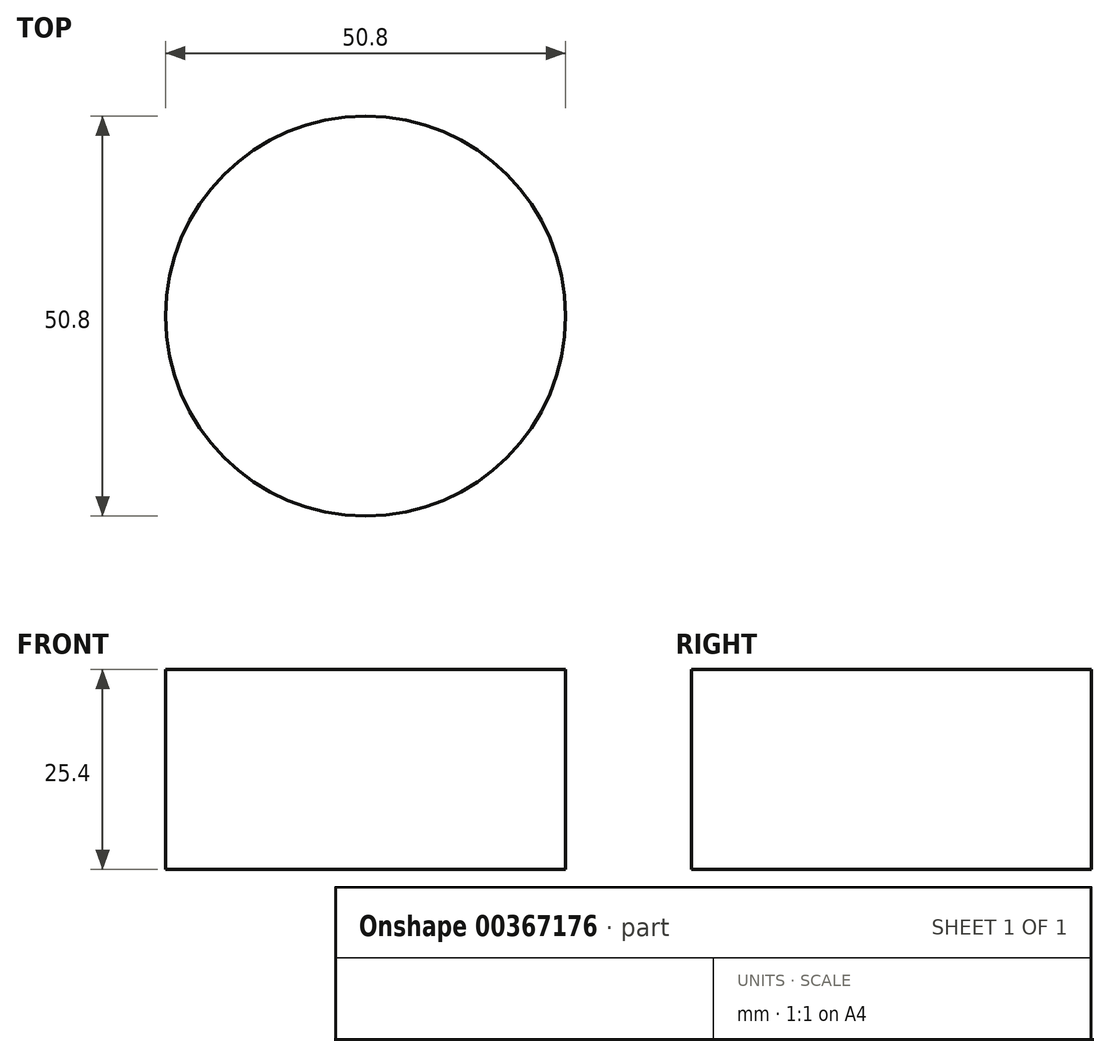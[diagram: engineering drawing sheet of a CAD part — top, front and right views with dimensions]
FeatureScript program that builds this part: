
annotation { "Feature Type Name" : "Feature", "Feature Type Description" : "" }
export const myFeature = defineFeature(function(context is Context, id is Id, definition is map)
    precondition{}
    {
        {
            var Q0;
            Q0=qCreatedBy(makeId("Top.planeOp"),FACE);
            var sketch = newSketch(context, id + "F0", { "sketchPlane" : qUnion([Q0])});
            skCircle(sketch, "E0", {"center": v(0, 0) * mm, "radius": 25.4 * mm});
            skSolve(sketch);
        }
        {
            var Q0;
            Q0=makeQuery(id+"F0.imprint","IMPRINT",FACE,{"disambiguationData":[TD([[makeQuery(id+"F0.imprint","IMPRINT",EDGE,{"derivedFrom":sQuery(id+"F0.wireOp",EDGE,"E0")}),1.0]])]});
            extrude(context, id + "F1", {"entities" : qUnion([Q0]), "depth" : 25.4 * mm});
        }
    });
